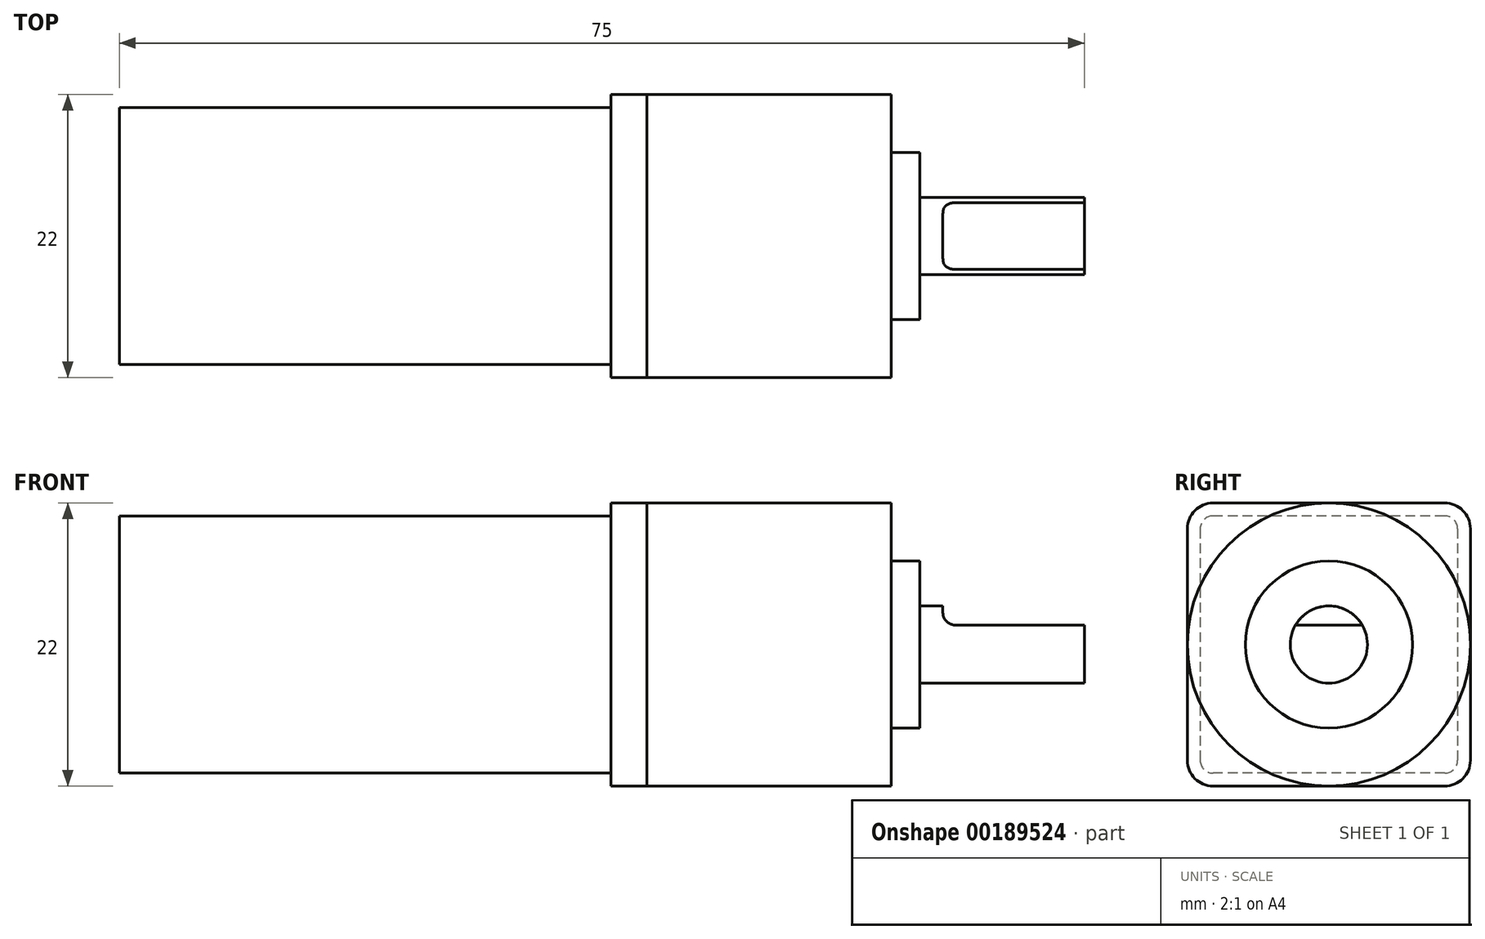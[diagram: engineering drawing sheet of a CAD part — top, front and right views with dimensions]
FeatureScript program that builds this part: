
annotation { "Feature Type Name" : "Feature", "Feature Type Description" : "" }
export const myFeature = defineFeature(function(context is Context, id is Id, definition is map)
    precondition{}
    {
        {
            var Q0;
            Q0=qCreatedBy(makeId("Top.planeOp"),FACE);
            var sketch = newSketch(context, id + "F0", { "sketchPlane" : qUnion([Q0])});
            skLineSegment(sketch, "E0.bottom", {"start": v(0, -11) * mm, "end": v(2.8, -11) * mm});
            skLineSegment(sketch, "E0.top", {"start": v(0, 11) * mm, "end": v(2.8, 11) * mm});
            skLineSegment(sketch, "E0.left", {"start": v(0, -11) * mm, "end": v(0, 11) * mm});
            skLineSegment(sketch, "E0.right", {"start": v(2.8, -11) * mm, "end": v(2.8, 11) * mm});
            skSolve(sketch);
        }
        {
            var Q0;
            Q0 = qSketchRegion(id + "F0", true);
            extrude(context, id + "F1", {"entities" : qUnion([Q0]), "endBound" : BoundingType.SYMMETRIC, "depth" : 22 * mm});
        }
        {
            var Q0;
            Q0=makeQuery(id+"F1.opExtrude","CAP_EDGE",EDGE,{"disambiguationData":[OSD([sQuery(id+"F0.wireOp",EDGE,"E0.bottom")])],"isStart":false});
            var Q1;
            Q1=makeQuery(id+"F1.opExtrude","CAP_EDGE",EDGE,{"disambiguationData":[OSD([sQuery(id+"F0.wireOp",EDGE,"E0.top")])],"isStart":false});
            var Q2;
            Q2=makeQuery(id+"F1.opExtrude","CAP_EDGE",EDGE,{"disambiguationData":[OSD([sQuery(id+"F0.wireOp",EDGE,"E0.bottom")])],"isStart":true});
            var Q3;
            Q3=makeQuery(id+"F1.opExtrude","CAP_EDGE",EDGE,{"disambiguationData":[OSD([sQuery(id+"F0.wireOp",EDGE,"E0.top")])],"isStart":true});
            fillet(context, id + "F2", {"entities" : qUnion([Q0, Q1, Q2, Q3]), "radius" : 2 * mm, "tangentPropagation" : true, "allowEdgeOverflow" : false});
        }
        {
            var Q0;
            Q0=makeQuery(id+"F1.opExtrude","SWEPT_FACE",FACE,{"disambiguationData":[OSD([sQuery(id+"F0.wireOp",EDGE,"E0.right")])]});
            var sketch = newSketch(context, id + "F3", { "sketchPlane" : qUnion([Q0])});
            skCircle(sketch, "E1", {"center": v(0, 0) * mm, "radius": 11 * mm});
            skSolve(sketch);
        }
        {
            var Q0;
            Q0=makeQuery(id+"F3.imprint","IMPRINT",FACE,{"disambiguationData":[TD([[makeQuery(id+"F3.imprint","IMPRINT",EDGE,{"derivedFrom":sQuery(id+"F3.wireOp",EDGE,"E1")}),1.0]])]});
            var Q1;
            {var subQ0=sQuery(id+"F3.wireOp",EDGE,"E1");var subQ1=makeQuery(id+"F1.opExtrude","CAP_EDGE",EDGE,{"disambiguationData":[OSD([sQuery(id+"F0.wireOp",EDGE,"E0.right")])],"isStart":false});var subQ2=makeQuery(id+"F3.imprint","INTERSECT",VERTEX,{"disambiguationData":[OD(0.0)],"derivedFrom":[subQ1,subQ0]});Q1=makeQuery(id+"F3.imprint","IMPRINT",FACE,{"disambiguationData":[TD([[makeQuery(id+"F3.imprint","IMPRINT",EDGE,{"disambiguationData":[TD([[subQ2,-1.0]])],"derivedFrom":subQ0}),1.0]])]});}
            var Q2;
            {var subQ0=sQuery(id+"F3.wireOp",EDGE,"E1");var subQ1=makeQuery(id+"F1.opExtrude","SWEPT_EDGE",EDGE,{"disambiguationData":[OSD([sQuery(id+"F0.wireOp",EDGE,"E0.bottom"),sQuery(id+"F0.wireOp",EDGE,"E0.right")])]});var subQ2=makeQuery(id+"F3.imprint","INTERSECT",VERTEX,{"disambiguationData":[OD(0.0)],"derivedFrom":[subQ1,subQ0]});Q2=makeQuery(id+"F3.imprint","IMPRINT",FACE,{"disambiguationData":[TD([[makeQuery(id+"F3.imprint","IMPRINT",EDGE,{"disambiguationData":[TD([[subQ2,-1.0]])],"derivedFrom":subQ0}),1.0]])]});}
            var Q3;
            {var subQ0=sQuery(id+"F3.wireOp",EDGE,"E1");var subQ1=makeQuery(id+"F1.opExtrude","CAP_EDGE",EDGE,{"disambiguationData":[OSD([sQuery(id+"F0.wireOp",EDGE,"E0.right")])],"isStart":true});var subQ2=makeQuery(id+"F3.imprint","INTERSECT",VERTEX,{"disambiguationData":[OD(0.0)],"derivedFrom":[subQ1,subQ0]});Q3=makeQuery(id+"F3.imprint","IMPRINT",FACE,{"disambiguationData":[TD([[makeQuery(id+"F3.imprint","IMPRINT",EDGE,{"disambiguationData":[TD([[subQ2,-1.0]])],"derivedFrom":subQ0}),1.0]])]});}
            var Q4;
            {var subQ0=sQuery(id+"F3.wireOp",EDGE,"E1");var subQ1=makeQuery(id+"F1.opExtrude","SWEPT_EDGE",EDGE,{"disambiguationData":[OSD([sQuery(id+"F0.wireOp",EDGE,"E0.top"),sQuery(id+"F0.wireOp",EDGE,"E0.right")])]});var subQ2=makeQuery(id+"F3.imprint","INTERSECT",VERTEX,{"disambiguationData":[OD(0.0)],"derivedFrom":[subQ1,subQ0]});Q4=makeQuery(id+"F3.imprint","IMPRINT",FACE,{"disambiguationData":[TD([[makeQuery(id+"F3.imprint","IMPRINT",EDGE,{"disambiguationData":[TD([[subQ2,1.0]])],"derivedFrom":subQ0}),1.0]])]});}
            extrude(context, id + "F4", {"entities" : qUnion([Q0, Q1, Q2, Q3, Q4]), "operationType" : NewBodyOperationType.ADD, "depth" : 19 * mm});
        }
        {
            var Q0;
            Q0=makeQuery(id+"F4.opExtrude","CAP_FACE",FACE,{"disambiguationData":[OSD([sQuery(id+"F3.wireOp",EDGE,"E1")])],"isStart":false});
            var sketch = newSketch(context, id + "F5", { "sketchPlane" : qUnion([Q0])});
            skCircle(sketch, "E2", {"center": v(0, 0) * mm, "radius": 3 * mm});
            skCircle(sketch, "E3", {"center": v(0, 0) * mm, "radius": 6.5 * mm});
            skSolve(sketch);
        }
        {
            var Q0;
            Q0=makeQuery(id+"F5.imprint","IMPRINT",FACE,{"disambiguationData":[TD([[makeQuery(id+"F5.imprint","IMPRINT",EDGE,{"derivedFrom":sQuery(id+"F5.wireOp",EDGE,"E2")}),1.0]])]});
            extrude(context, id + "F6", {"entities" : qUnion([Q0]), "operationType" : NewBodyOperationType.ADD, "depth" : 15 * mm});
        }
        {
            var Q0;
            Q0=makeQuery(id+"F6.opExtrude","CAP_FACE",FACE,{"disambiguationData":[OSD([sQuery(id+"F5.wireOp",EDGE,"E2")])],"isStart":false});
            var sketch = newSketch(context, id + "F7", { "sketchPlane" : qUnion([Q0])});
            skLineSegment(sketch, "E4", {"start": v(-2.6, 1.5) * mm, "end": v(2.6, 1.5) * mm});
            skSolve(sketch);
        }
        {
            var Q0;
            {var subQ0=sQuery(id+"F7.wireOp",EDGE,"E4");Q0=makeQuery(id+"F7.imprint","IMPRINT",FACE,{"disambiguationData":[TD([[makeQuery(id+"F7.imprint","IMPRINT",EDGE,{"derivedFrom":subQ0}),1.0]])]});}
            extrude(context, id + "F8", {"entities" : qUnion([Q0]), "operationType" : NewBodyOperationType.REMOVE, "oppositeDirection" : true, "depth" : 11 * mm});
        }
        {
            var Q0;
            Q0=makeQuery(id+"F8.boolean.opBoolean","COPY",EDGE,{"derivedFrom":makeQuery(id+"F8.opExtrude","CAP_EDGE",EDGE,{"disambiguationData":[OSD([sQuery(id+"F7.wireOp",EDGE,"E4")])],"isStart":false})});
            fillet(context, id + "F9", {"entities" : qUnion([Q0]), "radius" : 1 * mm, "tangentPropagation" : true, "allowEdgeOverflow" : false});
        }
        {
            var Q0;
            Q0=makeQuery(id+"F1.opExtrude","SWEPT_FACE",FACE,{"disambiguationData":[OSD([sQuery(id+"F0.wireOp",EDGE,"E0.left")])]});
            var sketch = newSketch(context, id + "F10", { "sketchPlane" : qUnion([Q0])});
            skLineSegment(sketch, "E5.bottom", {"start": v(-10, 10) * mm, "end": v(10, 10) * mm});
            skLineSegment(sketch, "E5.top", {"start": v(-10, -10) * mm, "end": v(10, -10) * mm});
            skLineSegment(sketch, "E5.left", {"start": v(-10, 10) * mm, "end": v(-10, -10) * mm});
            skLineSegment(sketch, "E5.right", {"start": v(10, 10) * mm, "end": v(10, -10) * mm});
            skSolve(sketch);
        }
        {
            var Q0;
            Q0=makeQuery(id+"F10.imprint","IMPRINT",FACE,{"disambiguationData":[TD([[makeQuery(id+"F10.imprint","IMPRINT",EDGE,{"derivedFrom":sQuery(id+"F10.wireOp",EDGE,"E5.bottom")}),-1.0]])]});
            extrude(context, id + "F11", {"entities" : qUnion([Q0]), "operationType" : NewBodyOperationType.ADD, "depth" : (41 - 2.8) * mm});
        }
        {
            var Q0;
            Q0=makeQuery(id+"F11.opExtrude","SWEPT_EDGE",EDGE,{"disambiguationData":[OSD([sQuery(id+"F10.wireOp",EDGE,"E5.bottom"),sQuery(id+"F10.wireOp",EDGE,"E5.right")])]});
            var Q1;
            Q1=makeQuery(id+"F11.opExtrude","SWEPT_EDGE",EDGE,{"disambiguationData":[OSD([sQuery(id+"F10.wireOp",EDGE,"E5.bottom"),sQuery(id+"F10.wireOp",EDGE,"E5.left")])]});
            var Q2;
            Q2=makeQuery(id+"F11.opExtrude","SWEPT_EDGE",EDGE,{"disambiguationData":[OSD([sQuery(id+"F10.wireOp",EDGE,"E5.top"),sQuery(id+"F10.wireOp",EDGE,"E5.right")])]});
            var Q3;
            Q3=makeQuery(id+"F11.opExtrude","SWEPT_EDGE",EDGE,{"disambiguationData":[OSD([sQuery(id+"F10.wireOp",EDGE,"E5.top"),sQuery(id+"F10.wireOp",EDGE,"E5.left")])]});
            fillet(context, id + "F12", {"entities" : qUnion([Q0, Q1, Q2, Q3]), "radius" : 1 * mm, "tangentPropagation" : true, "allowEdgeOverflow" : false});
        }
        {
            var Q0;
            Q0=makeQuery(id+"F5.imprint","IMPRINT",FACE,{"disambiguationData":[TD([[makeQuery(id+"F5.imprint","IMPRINT",EDGE,{"derivedFrom":sQuery(id+"F5.wireOp",EDGE,"E2")}),-1.0]])]});
            extrude(context, id + "F13", {"entities" : qUnion([Q0]), "operationType" : NewBodyOperationType.ADD, "depth" : 2.2 * mm});
        }
    });
